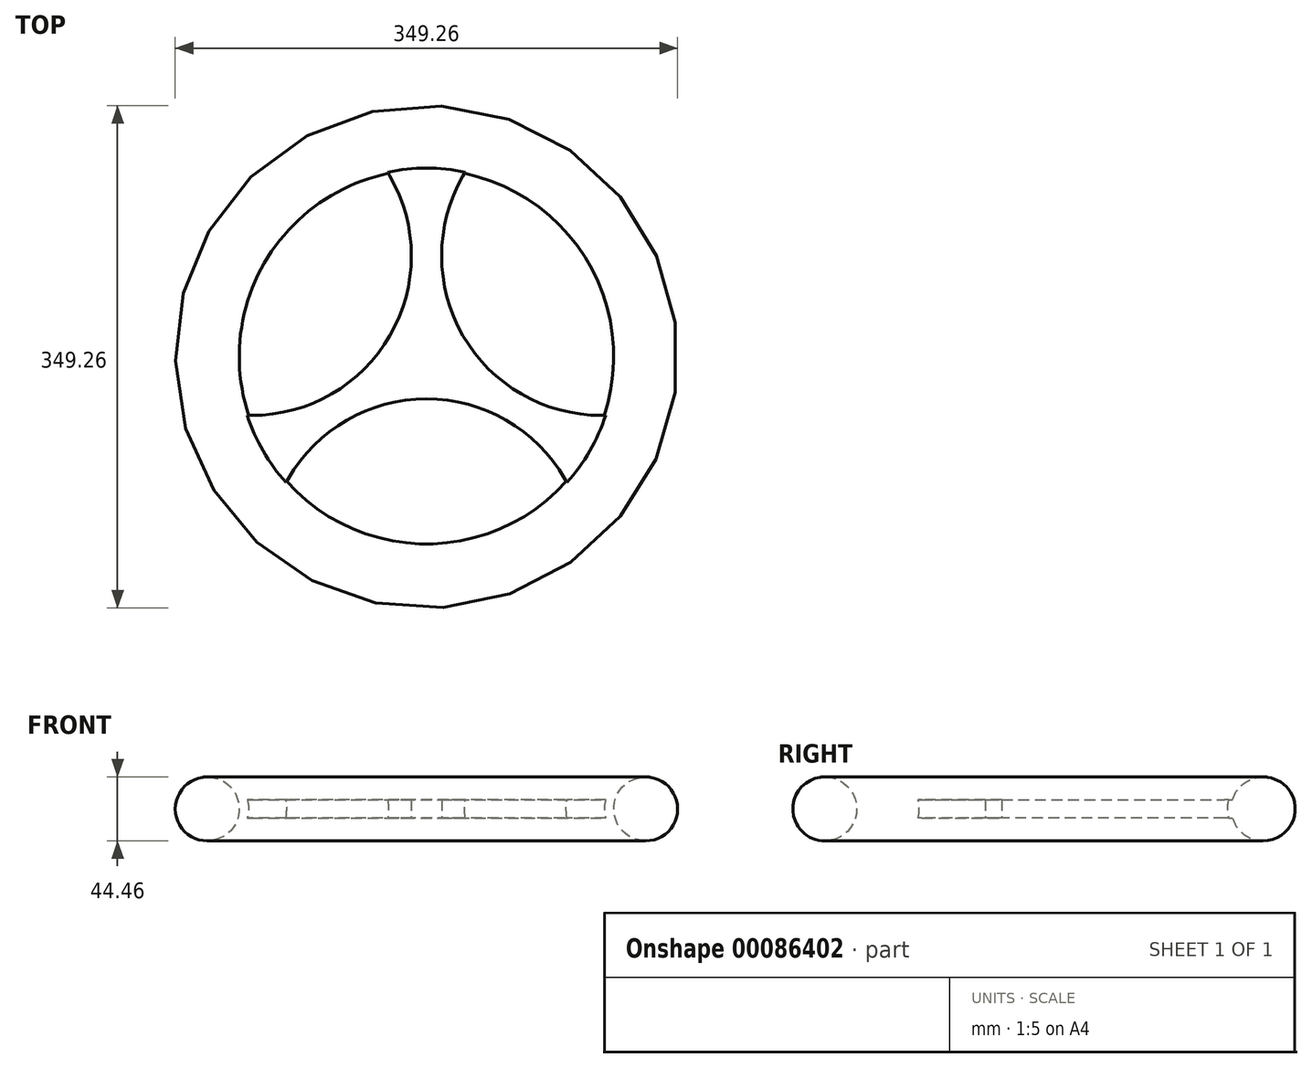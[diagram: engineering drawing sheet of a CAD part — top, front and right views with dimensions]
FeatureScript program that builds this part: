
annotation { "Feature Type Name" : "Feature", "Feature Type Description" : "" }
export const myFeature = defineFeature(function(context is Context, id is Id, definition is map)
    precondition{}
    {
        {
            var Q0;
            Q0=qCreatedBy(makeId("Top.planeOp"),FACE);
            var sketch = newSketch(context, id + "F0", { "sketchPlane" : qUnion([Q0])});
            skCircle(sketch, "E0", {"center": v(0, 0) * mm, "radius": 152.4 * mm});
            skLineSegment(sketch, "E1", {"start": v(0, 152.4) * mm, "end": v(0, -152.4) * mm, "construction": true});
            skLineSegment(sketch, "E2", {"start": v(0, 0) * mm, "end": v(-131.98, -76.2) * mm, "construction": true});
            skLineSegment(sketch, "E3", {"start": v(0, 0) * mm, "end": v(131.98, -76.2) * mm, "construction": true});
            skLineSegment(sketch, "E4", {"start": v(-38.1, 147.56) * mm, "end": v(-25.4, 125.56) * mm});
            skLineSegment(sketch, "E5", {"start": v(-25.4, 125.56) * mm, "end": v(25.4, 125.56) * mm, "construction": true});
            skLineSegment(sketch, "E6", {"start": v(25.4, 125.56) * mm, "end": v(38.1, 147.56) * mm});
            skLineSegment(sketch, "E7", {"start": v(-146.84, -40.78) * mm, "end": v(-121.44, -40.78) * mm});
            skLineSegment(sketch, "E8", {"start": v(-121.44, -40.78) * mm, "end": v(-96.04, -84.78) * mm, "construction": true});
            skLineSegment(sketch, "E9", {"start": v(-96.04, -84.78) * mm, "end": v(-108.74, -106.78) * mm});
            skLineSegment(sketch, "E10", {"start": v(146.84, -40.78) * mm, "end": v(121.44, -40.78) * mm});
            skLineSegment(sketch, "E11", {"start": v(121.44, -40.78) * mm, "end": v(96.04, -84.78) * mm, "construction": true});
            skLineSegment(sketch, "E12", {"start": v(96.04, -84.78) * mm, "end": v(108.74, -106.78) * mm});
            skArc(sketch, "E13", {"start": v(-121.44, -40.78) * mm, "mid": v(-25.4, 14.66) * mm, "end": v(-25.4, 125.56) * mm});
            skArc(sketch, "E14", {"start": v(25.4, 125.56) * mm, "mid": v(25.4, 14.66) * mm, "end": v(121.44, -40.78) * mm});
            skArc(sketch, "E15", {"start": v(96.04, -84.78) * mm, "mid": v(0, -29.33) * mm, "end": v(-96.04, -84.78) * mm});
            skSolve(sketch);
        }
        {
            var Q0;
            Q0=qCreatedBy(makeId("Right.planeOp"),FACE);
            var sketch = newSketch(context, id + "F1", { "sketchPlane" : qUnion([Q0])});
            skLineSegment(sketch, "E16", {"start": v(0, 0) * mm, "end": v(152.4, 0) * mm, "construction": true});
            skCircle(sketch, "E17", {"center": v(152.4, 0) * mm, "radius": 22.23 * mm});
            skSolve(sketch);
        }
        {
            var Q0;
            {var subQ4=sQuery(id+"F0.wireOp",EDGE,"E4");Q0=makeQuery(id+"F0.imprint","IMPRINT",FACE,{"disambiguationData":[TD([[makeQuery(id+"F0.imprint","IMPRINT",EDGE,{"derivedFrom":subQ4}),1.0]])]});}
            extrude(context, id + "F2", {"entities" : qUnion([Q0]), "depth" : 6.35 * mm, "hasSecondDirection" : true, "secondDirectionOppositeDirection" : true, "secondDirectionDepth" : 6.35 * mm});
        }
        {
            var Q0;
            Q0=makeQuery(id+"F1.imprint","IMPRINT",FACE,{"disambiguationData":[TD([[makeQuery(id+"F1.imprint","IMPRINT",EDGE,{"derivedFrom":sQuery(id+"F1.wireOp",EDGE,"E17")}),1.0]])]});
            var Q1;
            Q1=sQuery(id+"F0.wireOp",EDGE,"E0");
            sweep(context, id + "F3", {"operationType" : NewBodyOperationType.ADD, "profiles" : qUnion([Q0]), "path" : qUnion([Q1])});
        }
    });
